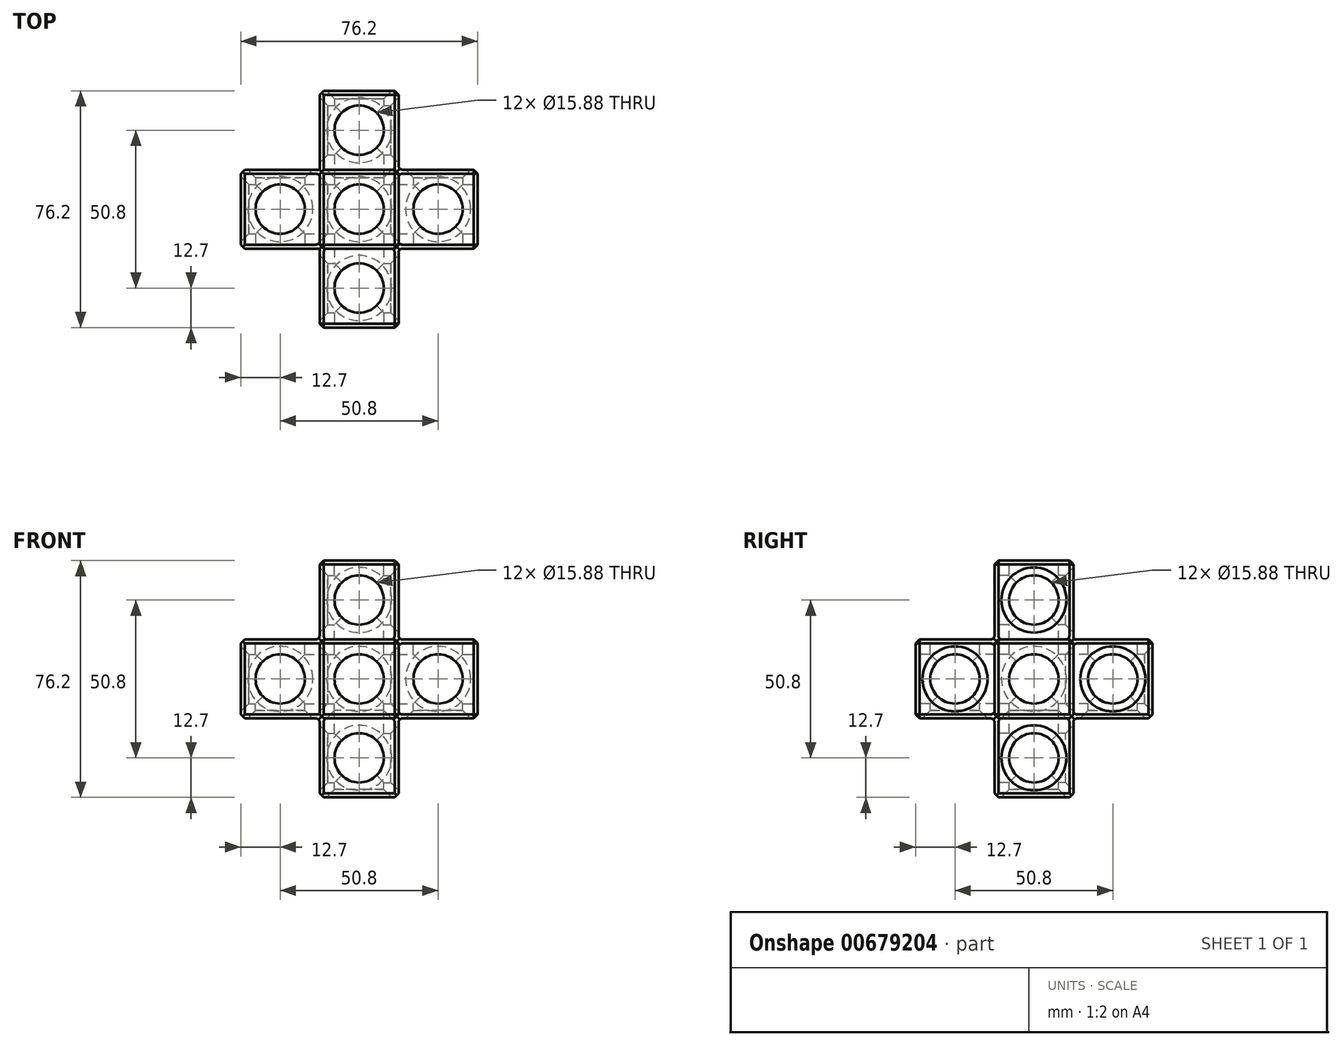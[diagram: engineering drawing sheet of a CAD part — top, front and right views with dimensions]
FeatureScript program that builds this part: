
annotation { "Feature Type Name" : "Feature", "Feature Type Description" : "" }
export const myFeature = defineFeature(function(context is Context, id is Id, definition is map)
    precondition{}
    {
        {
            var Q0;
            Q0=qCreatedBy(makeId("Front.planeOp"),FACE);
            var sketch = newSketch(context, id + "F0", { "sketchPlane" : qUnion([Q0])});
            skLineSegment(sketch, "E0", {"start": v(0, 0) * mm, "end": v(25.4, 0) * mm});
            skLineSegment(sketch, "E1", {"start": v(25.4, 0) * mm, "end": v(25.4, 25.4) * mm});
            skLineSegment(sketch, "E2", {"start": v(25.4, 25.4) * mm, "end": v(50.8, 25.4) * mm});
            skLineSegment(sketch, "E3", {"start": v(50.8, 25.4) * mm, "end": v(50.8, 0) * mm});
            skLineSegment(sketch, "E4", {"start": v(50.8, 0) * mm, "end": v(76.2, 0) * mm});
            skLineSegment(sketch, "E5", {"start": v(76.2, 0) * mm, "end": v(76.2, -25.4) * mm});
            skLineSegment(sketch, "E6", {"start": v(76.2, -25.4) * mm, "end": v(50.8, -25.4) * mm});
            skLineSegment(sketch, "E7", {"start": v(50.8, -25.4) * mm, "end": v(50.8, -50.8) * mm});
            skLineSegment(sketch, "E8", {"start": v(50.8, -50.8) * mm, "end": v(25.4, -50.8) * mm});
            skLineSegment(sketch, "E9", {"start": v(25.4, -50.8) * mm, "end": v(25.4, -25.4) * mm});
            skLineSegment(sketch, "E10", {"start": v(25.4, -25.4) * mm, "end": v(0, -25.4) * mm});
            skLineSegment(sketch, "E11", {"start": v(0, -25.4) * mm, "end": v(0, 0) * mm});
            skSolve(sketch);
        }
        {
            var Q0;
            Q0 = qSketchRegion(id + "F0", true);
            extrude(context, id + "F1", {"entities" : qUnion([Q0]), "depth" : 25.4 * mm, "offsetDistance" : 25.4 * mm});
        }
        {
            var Q0;
            Q0=makeQuery(id+"F1.opExtrude","CAP_FACE",FACE,{"disambiguationData":[OSD([sQuery(id+"F0.wireOp",EDGE,"E0"),sQuery(id+"F0.wireOp",EDGE,"E1"),sQuery(id+"F0.wireOp",EDGE,"E2"),sQuery(id+"F0.wireOp",EDGE,"E3"),sQuery(id+"F0.wireOp",EDGE,"E4"),sQuery(id+"F0.wireOp",EDGE,"E5"),sQuery(id+"F0.wireOp",EDGE,"E6"),sQuery(id+"F0.wireOp",EDGE,"E7"),sQuery(id+"F0.wireOp",EDGE,"E8"),sQuery(id+"F0.wireOp",EDGE,"E9"),sQuery(id+"F0.wireOp",EDGE,"E10"),sQuery(id+"F0.wireOp",EDGE,"E11")])],"isStart":false});
            var sketch = newSketch(context, id + "F2", { "sketchPlane" : qUnion([Q0])});
            skLineSegment(sketch, "E12.bottom", {"start": v(25.4, 0) * mm, "end": v(50.8, 0) * mm});
            skLineSegment(sketch, "E12.top", {"start": v(25.4, -25.4) * mm, "end": v(50.8, -25.4) * mm});
            skLineSegment(sketch, "E12.left", {"start": v(25.4, 0) * mm, "end": v(25.4, -25.4) * mm});
            skLineSegment(sketch, "E12.right", {"start": v(50.8, 0) * mm, "end": v(50.8, -25.4) * mm});
            skSolve(sketch);
        }
        {
            var Q0;
            Q0 = qSketchRegion(id + "F2", true);
            extrude(context, id + "F3", {"entities" : qUnion([Q0]), "operationType" : NewBodyOperationType.ADD, "depth" : 25.4 * mm, "offsetDistance" : 25.4 * mm});
        }
        {
            var Q0;
            Q0=makeQuery(id+"F1.opExtrude","CAP_FACE",FACE,{"disambiguationData":[OSD([sQuery(id+"F0.wireOp",EDGE,"E0"),sQuery(id+"F0.wireOp",EDGE,"E1"),sQuery(id+"F0.wireOp",EDGE,"E2"),sQuery(id+"F0.wireOp",EDGE,"E3"),sQuery(id+"F0.wireOp",EDGE,"E4"),sQuery(id+"F0.wireOp",EDGE,"E5"),sQuery(id+"F0.wireOp",EDGE,"E6"),sQuery(id+"F0.wireOp",EDGE,"E7"),sQuery(id+"F0.wireOp",EDGE,"E8"),sQuery(id+"F0.wireOp",EDGE,"E9"),sQuery(id+"F0.wireOp",EDGE,"E10"),sQuery(id+"F0.wireOp",EDGE,"E11")])],"isStart":true});
            var sketch = newSketch(context, id + "F4", { "sketchPlane" : qUnion([Q0])});
            skLineSegment(sketch, "E13.bottom", {"start": v(-50.8, 0) * mm, "end": v(-25.4, 0) * mm});
            skLineSegment(sketch, "E13.top", {"start": v(-50.8, -25.4) * mm, "end": v(-25.4, -25.4) * mm});
            skLineSegment(sketch, "E13.left", {"start": v(-50.8, 0) * mm, "end": v(-50.8, -25.4) * mm});
            skLineSegment(sketch, "E13.right", {"start": v(-25.4, 0) * mm, "end": v(-25.4, -25.4) * mm});
            skSolve(sketch);
        }
        {
            var Q0;
            Q0 = qSketchRegion(id + "F4", true);
            extrude(context, id + "F5", {"entities" : qUnion([Q0]), "operationType" : NewBodyOperationType.ADD, "depth" : 25.4 * mm, "offsetDistance" : 25.4 * mm});
        }
        {
            var Q0;
            Q0=makeQuery(id+"F3.opExtrude","CAP_FACE",FACE,{"disambiguationData":[OSD([sQuery(id+"F2.wireOp",EDGE,"E12.bottom"),sQuery(id+"F2.wireOp",EDGE,"E12.top"),sQuery(id+"F2.wireOp",EDGE,"E12.left"),sQuery(id+"F2.wireOp",EDGE,"E12.right")])],"isStart":false});
            var sketch = newSketch(context, id + "F6", { "sketchPlane" : qUnion([Q0])});
            skCircle(sketch, "E14", {"center": v(38.1, -12.7) * mm, "radius": 7.94 * mm});
            skSolve(sketch);
        }
        {
            var Q0;
            Q0 = qSketchRegion(id + "F6", true);
            extrude(context, id + "F7", {"entities" : qUnion([Q0]), "operationType" : NewBodyOperationType.REMOVE, "endBound" : BoundingType.THROUGH_ALL, "oppositeDirection" : true, "depth" : 25.4 * mm, "offsetDistance" : 25.4 * mm});
        }
        {
            var Q0;
            Q0=makeQuery(id+"F1.opExtrude","SWEPT_FACE",FACE,{"disambiguationData":[OSD([sQuery(id+"F0.wireOp",EDGE,"E2")])]});
            var sketch = newSketch(context, id + "F8", { "sketchPlane" : qUnion([Q0])});
            skCircle(sketch, "E15", {"center": v(38.1, -12.7) * mm, "radius": 7.94 * mm});
            skSolve(sketch);
        }
        {
            var Q0;
            Q0 = qSketchRegion(id + "F8", true);
            extrude(context, id + "F9", {"entities" : qUnion([Q0]), "operationType" : NewBodyOperationType.REMOVE, "endBound" : BoundingType.THROUGH_ALL, "oppositeDirection" : true, "depth" : 25.4 * mm, "offsetDistance" : 25.4 * mm});
        }
        {
            var Q0;
            {var subQ0=sQuery(id+"F0.wireOp",EDGE,"E2");var subQ1=sQuery(id+"F0.wireOp",EDGE,"E1");var subQ2=sQuery(id+"F0.wireOp",EDGE,"E4");var subQ3=sQuery(id+"F0.wireOp",EDGE,"E3");var subQ4=sQuery(id+"F0.wireOp",EDGE,"E0");var subQ5=makeQuery(id+"F1.opExtrude","CAP_FACE",FACE,{"disambiguationData":[OSD([subQ4,subQ1,subQ0,subQ3,subQ2,sQuery(id+"F0.wireOp",EDGE,"E5"),sQuery(id+"F0.wireOp",EDGE,"E6"),sQuery(id+"F0.wireOp",EDGE,"E7"),sQuery(id+"F0.wireOp",EDGE,"E8"),sQuery(id+"F0.wireOp",EDGE,"E9"),sQuery(id+"F0.wireOp",EDGE,"E10"),sQuery(id+"F0.wireOp",EDGE,"E11")])],"isStart":false});Q0=makeQuery(id+"F3.boolean.opBoolean","SPLIT",FACE,{"disambiguationData":[TD([makeQuery(id+"F1.opExtrude","SWEPT_FACE",FACE,{"disambiguationData":[OSD([subQ0])]})])],"derivedFrom":subQ5});}
            var sketch = newSketch(context, id + "F10", { "sketchPlane" : qUnion([Q0])});
            skCircle(sketch, "E16", {"center": v(38.1, 12.7) * mm, "radius": 7.94 * mm});
            skCircle(sketch, "E17", {"center": v(63.5, -12.7) * mm, "radius": 7.94 * mm});
            skCircle(sketch, "E18", {"center": v(38.1, -38.1) * mm, "radius": 7.94 * mm});
            skCircle(sketch, "E19", {"center": v(12.7, -12.7) * mm, "radius": 7.94 * mm});
            skSolve(sketch);
        }
        {
            var Q0;
            Q0 = qSketchRegion(id + "F10", true);
            extrude(context, id + "F11", {"entities" : qUnion([Q0]), "operationType" : NewBodyOperationType.REMOVE, "endBound" : BoundingType.THROUGH_ALL, "oppositeDirection" : true, "depth" : 25.4 * mm, "offsetDistance" : 25.4 * mm});
        }
        {
            var Q0;
            Q0=makeQuery(id+"F1.opExtrude","SWEPT_FACE",FACE,{"disambiguationData":[OSD([sQuery(id+"F0.wireOp",EDGE,"E0")])]});
            var sketch = newSketch(context, id + "F12", { "sketchPlane" : qUnion([Q0])});
            skCircle(sketch, "E20", {"center": v(12.7, -12.7) * mm, "radius": 7.94 * mm});
            skPoint(sketch, "E20.centerSnap0", {"position": v(0, -12.7) * mm});
            skCircle(sketch, "E21", {"center": v(63.5, -12.7) * mm, "radius": 7.94 * mm});
            skCircle(sketch, "E22", {"center": v(38.1, -38.1) * mm, "radius": 7.94 * mm});
            skCircle(sketch, "E23", {"center": v(38.1, 12.7) * mm, "radius": 7.94 * mm});
            skSolve(sketch);
        }
        {
            var Q0;
            Q0 = qSketchRegion(id + "F12", true);
            extrude(context, id + "F13", {"entities" : qUnion([Q0]), "operationType" : NewBodyOperationType.REMOVE, "endBound" : BoundingType.THROUGH_ALL, "oppositeDirection" : true, "depth" : 25.4 * mm, "offsetDistance" : 25.4 * mm});
        }
        {
            var Q0;
            Q0=makeQuery(id+"F1.opExtrude","SWEPT_FACE",FACE,{"disambiguationData":[OSD([sQuery(id+"F0.wireOp",EDGE,"E5")])]});
            var sketch = newSketch(context, id + "F14", { "sketchPlane" : qUnion([Q0])});
            skCircle(sketch, "E24", {"center": v(-12.7, -12.7) * mm, "radius": 7.94 * mm});
            skPoint(sketch, "E24.centerSnap0", {"position": v(-12.7, 0) * mm});
            skPoint(sketch, "E24.centerSnap1", {"position": v(-25.4, -12.7) * mm});
            skCircle(sketch, "E25", {"center": v(-12.7, 12.7) * mm, "radius": 7.94 * mm});
            skCircle(sketch, "E26", {"center": v(-38.1, -12.7) * mm, "radius": 7.94 * mm});
            skCircle(sketch, "E27", {"center": v(12.7, -12.7) * mm, "radius": 7.94 * mm});
            skCircle(sketch, "E28", {"center": v(-12.7, -38.1) * mm, "radius": 7.94 * mm});
            skSolve(sketch);
        }
        {
            var Q0;
            Q0 = qSketchRegion(id + "F14", true);
            extrude(context, id + "F15", {"entities" : qUnion([Q0]), "operationType" : NewBodyOperationType.REMOVE, "endBound" : BoundingType.THROUGH_ALL, "oppositeDirection" : true, "depth" : 25.4 * mm, "offsetDistance" : 25.4 * mm});
        }
        {
            var Q0;
            Q0=makeQuery(id+"F9.boolean.opBoolean","COPY",EDGE,{"derivedFrom":makeQuery(id+"F9.opExtrude","CAP_EDGE",EDGE,{"disambiguationData":[OSD([sQuery(id+"F8.wireOp",EDGE,"E15")])],"isStart":true})});
            var Q1;
            Q1=makeQuery(id+"F11.boolean.opBoolean","COPY",EDGE,{"derivedFrom":makeQuery(id+"F11.opExtrude","CAP_EDGE",EDGE,{"disambiguationData":[OSD([sQuery(id+"F10.wireOp",EDGE,"E16")])],"isStart":true})});
            var Q2;
            Q2=makeQuery(id+"F15.boolean.opBoolean","INTERSECT",EDGE,{"derivedFrom":[makeQuery(id+"F1.opExtrude","SWEPT_FACE",FACE,{"disambiguationData":[OSD([sQuery(id+"F0.wireOp",EDGE,"E3")])]}),makeQuery(id+"F15.opExtrude","SWEPT_FACE",FACE,{"disambiguationData":[OSD([sQuery(id+"F14.wireOp",EDGE,"E25")])]})]});
            var Q3;
            Q3=makeQuery(id+"F13.boolean.opBoolean","COPY",EDGE,{"derivedFrom":makeQuery(id+"F13.opExtrude","CAP_EDGE",EDGE,{"disambiguationData":[OSD([sQuery(id+"F12.wireOp",EDGE,"E22")])],"isStart":true})});
            var Q4;
            Q4=makeQuery(id+"F7.boolean.opBoolean","COPY",EDGE,{"derivedFrom":makeQuery(id+"F7.opExtrude","CAP_EDGE",EDGE,{"disambiguationData":[OSD([sQuery(id+"F6.wireOp",EDGE,"E14")])],"isStart":true})});
            var Q5;
            Q5=makeQuery(id+"F15.boolean.opBoolean","INTERSECT",EDGE,{"derivedFrom":[makeQuery(id+"F3.opExtrude","SWEPT_FACE",FACE,{"disambiguationData":[OSD([sQuery(id+"F2.wireOp",EDGE,"E12.right")])]}),makeQuery(id+"F15.opExtrude","SWEPT_FACE",FACE,{"disambiguationData":[OSD([sQuery(id+"F14.wireOp",EDGE,"E26")])]})]});
            var Q6;
            Q6=makeQuery(id+"F11.boolean.opBoolean","COPY",EDGE,{"derivedFrom":makeQuery(id+"F11.opExtrude","CAP_EDGE",EDGE,{"disambiguationData":[OSD([sQuery(id+"F10.wireOp",EDGE,"E18")])],"isStart":true})});
            var Q7;
            Q7=makeQuery(id+"F15.boolean.opBoolean","INTERSECT",EDGE,{"derivedFrom":[makeQuery(id+"F1.opExtrude","SWEPT_FACE",FACE,{"disambiguationData":[OSD([sQuery(id+"F0.wireOp",EDGE,"E7")])]}),makeQuery(id+"F15.opExtrude","SWEPT_FACE",FACE,{"disambiguationData":[OSD([sQuery(id+"F14.wireOp",EDGE,"E28")])]})]});
            var Q8;
            Q8=makeQuery(id+"F15.boolean.opBoolean","COPY",EDGE,{"derivedFrom":makeQuery(id+"F15.opExtrude","CAP_EDGE",EDGE,{"disambiguationData":[OSD([sQuery(id+"F14.wireOp",EDGE,"E24")])],"isStart":true})});
            var Q9;
            Q9=makeQuery(id+"F11.boolean.opBoolean","COPY",EDGE,{"derivedFrom":makeQuery(id+"F11.opExtrude","CAP_EDGE",EDGE,{"disambiguationData":[OSD([sQuery(id+"F10.wireOp",EDGE,"E17")])],"isStart":true})});
            var Q10;
            Q10=makeQuery(id+"F15.boolean.opBoolean","INTERSECT",EDGE,{"derivedFrom":[makeQuery(id+"F5.opExtrude","SWEPT_FACE",FACE,{"disambiguationData":[OSD([sQuery(id+"F4.wireOp",EDGE,"E13.left")])]}),makeQuery(id+"F15.opExtrude","SWEPT_FACE",FACE,{"disambiguationData":[OSD([sQuery(id+"F14.wireOp",EDGE,"E27")])]})]});
            var Q11;
            Q11=makeQuery(id+"F13.boolean.opBoolean","COPY",EDGE,{"derivedFrom":makeQuery(id+"F13.opExtrude","CAP_EDGE",EDGE,{"disambiguationData":[OSD([sQuery(id+"F12.wireOp",EDGE,"E23")])],"isStart":true})});
            var Q12;
            Q12=makeQuery(id+"F13.boolean.opBoolean","COPY",EDGE,{"derivedFrom":makeQuery(id+"F13.opExtrude","CAP_EDGE",EDGE,{"disambiguationData":[OSD([sQuery(id+"F12.wireOp",EDGE,"E21")])],"isStart":true})});
            var Q13;
            Q13=makeQuery(id+"F13.boolean.opBoolean","COPY",EDGE,{"derivedFrom":makeQuery(id+"F13.opExtrude","CAP_EDGE",EDGE,{"disambiguationData":[OSD([sQuery(id+"F12.wireOp",EDGE,"E20")])],"isStart":true})});
            var Q14;
            Q14=makeQuery(id+"F11.boolean.opBoolean","COPY",EDGE,{"derivedFrom":makeQuery(id+"F11.opExtrude","CAP_EDGE",EDGE,{"disambiguationData":[OSD([sQuery(id+"F10.wireOp",EDGE,"E19")])],"isStart":true})});
            chamfer(context, id + "F16", {"entities" : qUnion([Q0, Q1, Q2, Q3, Q4, Q5, Q6, Q7, Q8, Q9, Q10, Q11, Q12, Q13, Q14]), "width" : 2.54 * mm, "tangentPropagation" : true});
        }
        {
            var Q0;
            Q0=makeQuery(id+"F15.boolean.opBoolean","INTERSECT",EDGE,{"derivedFrom":[makeQuery(id+"F1.opExtrude","SWEPT_FACE",FACE,{"disambiguationData":[OSD([sQuery(id+"F0.wireOp",EDGE,"E1")])]}),makeQuery(id+"F15.opExtrude","SWEPT_FACE",FACE,{"disambiguationData":[OSD([sQuery(id+"F14.wireOp",EDGE,"E25")])]})]});
            var Q1;
            Q1=makeQuery(id+"F15.boolean.opBoolean","INTERSECT",EDGE,{"derivedFrom":[makeQuery(id+"F1.opExtrude","SWEPT_FACE",FACE,{"disambiguationData":[OSD([sQuery(id+"F0.wireOp",EDGE,"E11")])]}),makeQuery(id+"F15.opExtrude","SWEPT_FACE",FACE,{"disambiguationData":[OSD([sQuery(id+"F14.wireOp",EDGE,"E24")])]})]});
            var Q2;
            Q2=makeQuery(id+"F15.boolean.opBoolean","INTERSECT",EDGE,{"derivedFrom":[makeQuery(id+"F1.opExtrude","SWEPT_FACE",FACE,{"disambiguationData":[OSD([sQuery(id+"F0.wireOp",EDGE,"E9")])]}),makeQuery(id+"F15.opExtrude","SWEPT_FACE",FACE,{"disambiguationData":[OSD([sQuery(id+"F14.wireOp",EDGE,"E28")])]})]});
            var Q3;
            Q3=makeQuery(id+"F15.boolean.opBoolean","INTERSECT",EDGE,{"derivedFrom":[makeQuery(id+"F3.opExtrude","SWEPT_FACE",FACE,{"disambiguationData":[OSD([sQuery(id+"F2.wireOp",EDGE,"E12.left")])]}),makeQuery(id+"F15.opExtrude","SWEPT_FACE",FACE,{"disambiguationData":[OSD([sQuery(id+"F14.wireOp",EDGE,"E26")])]})]});
            chamfer(context, id + "F17", {"entities" : qUnion([Q0, Q1, Q2, Q3]), "width" : 2.54 * mm, "tangentPropagation" : true});
        }
        {
            var Q0;
            {var subQ0=sQuery(id+"F0.wireOp",EDGE,"E5");var subQ1=sQuery(id+"F0.wireOp",EDGE,"E3");var subQ2=sQuery(id+"F0.wireOp",EDGE,"E4");var subQ3=sQuery(id+"F0.wireOp",EDGE,"E7");var subQ4=sQuery(id+"F0.wireOp",EDGE,"E6");var subQ5=makeQuery(id+"F1.opExtrude","CAP_FACE",FACE,{"disambiguationData":[OSD([sQuery(id+"F0.wireOp",EDGE,"E0"),sQuery(id+"F0.wireOp",EDGE,"E1"),sQuery(id+"F0.wireOp",EDGE,"E2"),subQ1,subQ2,subQ0,subQ4,subQ3,sQuery(id+"F0.wireOp",EDGE,"E8"),sQuery(id+"F0.wireOp",EDGE,"E9"),sQuery(id+"F0.wireOp",EDGE,"E10"),sQuery(id+"F0.wireOp",EDGE,"E11")])],"isStart":true});Q0=makeQuery(id+"F11.boolean.opBoolean","INTERSECT",EDGE,{"derivedFrom":[makeQuery(id+"F5.boolean.opBoolean","SPLIT",FACE,{"disambiguationData":[TD([makeQuery(id+"F1.opExtrude","SWEPT_FACE",FACE,{"disambiguationData":[OSD([subQ0])]})])],"derivedFrom":subQ5}),makeQuery(id+"F11.opExtrude","SWEPT_FACE",FACE,{"disambiguationData":[OSD([sQuery(id+"F10.wireOp",EDGE,"E17")])]})]});}
            var Q1;
            Q1=makeQuery(id+"F13.boolean.opBoolean","INTERSECT",EDGE,{"derivedFrom":[makeQuery(id+"F1.opExtrude","SWEPT_FACE",FACE,{"disambiguationData":[OSD([sQuery(id+"F0.wireOp",EDGE,"E6")])]}),makeQuery(id+"F13.opExtrude","SWEPT_FACE",FACE,{"disambiguationData":[OSD([sQuery(id+"F12.wireOp",EDGE,"E21")])]})]});
            var Q2;
            Q2=makeQuery(id+"F9.boolean.opBoolean","INTERSECT",EDGE,{"derivedFrom":[makeQuery(id+"F1.opExtrude","SWEPT_FACE",FACE,{"disambiguationData":[OSD([sQuery(id+"F0.wireOp",EDGE,"E8")])]}),makeQuery(id+"F9.opExtrude","SWEPT_FACE",FACE,{"disambiguationData":[OSD([sQuery(id+"F8.wireOp",EDGE,"E15")])]})]});
            var Q3;
            {var subQ0=sQuery(id+"F0.wireOp",EDGE,"E8");var subQ1=sQuery(id+"F0.wireOp",EDGE,"E7");var subQ2=sQuery(id+"F0.wireOp",EDGE,"E6");var subQ3=sQuery(id+"F0.wireOp",EDGE,"E10");var subQ4=sQuery(id+"F0.wireOp",EDGE,"E9");var subQ5=makeQuery(id+"F1.opExtrude","CAP_FACE",FACE,{"disambiguationData":[OSD([sQuery(id+"F0.wireOp",EDGE,"E0"),sQuery(id+"F0.wireOp",EDGE,"E1"),sQuery(id+"F0.wireOp",EDGE,"E2"),sQuery(id+"F0.wireOp",EDGE,"E3"),sQuery(id+"F0.wireOp",EDGE,"E4"),sQuery(id+"F0.wireOp",EDGE,"E5"),subQ2,subQ1,subQ0,subQ4,subQ3,sQuery(id+"F0.wireOp",EDGE,"E11")])],"isStart":true});Q3=makeQuery(id+"F11.boolean.opBoolean","INTERSECT",EDGE,{"derivedFrom":[makeQuery(id+"F5.boolean.opBoolean","SPLIT",FACE,{"disambiguationData":[TD([makeQuery(id+"F1.opExtrude","SWEPT_FACE",FACE,{"disambiguationData":[OSD([subQ0])]})])],"derivedFrom":subQ5}),makeQuery(id+"F11.opExtrude","SWEPT_FACE",FACE,{"disambiguationData":[OSD([sQuery(id+"F10.wireOp",EDGE,"E18")])]})]});}
            var Q4;
            Q4=makeQuery(id+"F13.boolean.opBoolean","INTERSECT",EDGE,{"derivedFrom":[makeQuery(id+"F5.opExtrude","SWEPT_FACE",FACE,{"disambiguationData":[OSD([sQuery(id+"F4.wireOp",EDGE,"E13.top")])]}),makeQuery(id+"F13.opExtrude","SWEPT_FACE",FACE,{"disambiguationData":[OSD([sQuery(id+"F12.wireOp",EDGE,"E23")])]})]});
            var Q5;
            Q5=makeQuery(id+"F15.boolean.opBoolean","INTERSECT",EDGE,{"derivedFrom":[makeQuery(id+"F5.opExtrude","SWEPT_FACE",FACE,{"disambiguationData":[OSD([sQuery(id+"F4.wireOp",EDGE,"E13.right")])]}),makeQuery(id+"F15.opExtrude","SWEPT_FACE",FACE,{"disambiguationData":[OSD([sQuery(id+"F14.wireOp",EDGE,"E27")])]})]});
            var Q6;
            {var subQ0=sQuery(id+"F0.wireOp",EDGE,"E2");var subQ1=sQuery(id+"F0.wireOp",EDGE,"E1");var subQ2=sQuery(id+"F0.wireOp",EDGE,"E4");var subQ3=sQuery(id+"F0.wireOp",EDGE,"E3");var subQ4=sQuery(id+"F0.wireOp",EDGE,"E0");var subQ5=makeQuery(id+"F1.opExtrude","CAP_FACE",FACE,{"disambiguationData":[OSD([subQ4,subQ1,subQ0,subQ3,subQ2,sQuery(id+"F0.wireOp",EDGE,"E5"),sQuery(id+"F0.wireOp",EDGE,"E6"),sQuery(id+"F0.wireOp",EDGE,"E7"),sQuery(id+"F0.wireOp",EDGE,"E8"),sQuery(id+"F0.wireOp",EDGE,"E9"),sQuery(id+"F0.wireOp",EDGE,"E10"),sQuery(id+"F0.wireOp",EDGE,"E11")])],"isStart":true});Q6=makeQuery(id+"F11.boolean.opBoolean","INTERSECT",EDGE,{"derivedFrom":[makeQuery(id+"F5.boolean.opBoolean","SPLIT",FACE,{"disambiguationData":[TD([makeQuery(id+"F1.opExtrude","SWEPT_FACE",FACE,{"disambiguationData":[OSD([subQ0])]})])],"derivedFrom":subQ5}),makeQuery(id+"F11.opExtrude","SWEPT_FACE",FACE,{"disambiguationData":[OSD([sQuery(id+"F10.wireOp",EDGE,"E16")])]})]});}
            var Q7;
            {var subQ0=sQuery(id+"F0.wireOp",EDGE,"E1");var subQ1=sQuery(id+"F0.wireOp",EDGE,"E9");var subQ2=sQuery(id+"F0.wireOp",EDGE,"E0");var subQ3=sQuery(id+"F0.wireOp",EDGE,"E11");var subQ4=sQuery(id+"F0.wireOp",EDGE,"E10");var subQ5=makeQuery(id+"F1.opExtrude","CAP_FACE",FACE,{"disambiguationData":[OSD([subQ2,subQ0,sQuery(id+"F0.wireOp",EDGE,"E2"),sQuery(id+"F0.wireOp",EDGE,"E3"),sQuery(id+"F0.wireOp",EDGE,"E4"),sQuery(id+"F0.wireOp",EDGE,"E5"),sQuery(id+"F0.wireOp",EDGE,"E6"),sQuery(id+"F0.wireOp",EDGE,"E7"),sQuery(id+"F0.wireOp",EDGE,"E8"),subQ1,subQ4,subQ3])],"isStart":true});Q7=makeQuery(id+"F11.boolean.opBoolean","INTERSECT",EDGE,{"derivedFrom":[makeQuery(id+"F5.boolean.opBoolean","SPLIT",FACE,{"disambiguationData":[TD([makeQuery(id+"F1.opExtrude","SWEPT_FACE",FACE,{"disambiguationData":[OSD([subQ3])]})])],"derivedFrom":subQ5}),makeQuery(id+"F11.opExtrude","SWEPT_FACE",FACE,{"disambiguationData":[OSD([sQuery(id+"F10.wireOp",EDGE,"E19")])]})]});}
            var Q8;
            Q8=makeQuery(id+"F13.boolean.opBoolean","INTERSECT",EDGE,{"derivedFrom":[makeQuery(id+"F1.opExtrude","SWEPT_FACE",FACE,{"disambiguationData":[OSD([sQuery(id+"F0.wireOp",EDGE,"E10")])]}),makeQuery(id+"F13.opExtrude","SWEPT_FACE",FACE,{"disambiguationData":[OSD([sQuery(id+"F12.wireOp",EDGE,"E20")])]})]});
            var Q9;
            Q9=makeQuery(id+"F7.boolean.opBoolean","INTERSECT",EDGE,{"derivedFrom":[makeQuery(id+"F5.opExtrude","CAP_FACE",FACE,{"disambiguationData":[OSD([sQuery(id+"F4.wireOp",EDGE,"E13.bottom"),sQuery(id+"F4.wireOp",EDGE,"E13.top"),sQuery(id+"F4.wireOp",EDGE,"E13.left"),sQuery(id+"F4.wireOp",EDGE,"E13.right")])],"isStart":false}),makeQuery(id+"F7.opExtrude","SWEPT_FACE",FACE,{"disambiguationData":[OSD([sQuery(id+"F6.wireOp",EDGE,"E14")])]})]});
            chamfer(context, id + "F18", {"entities" : qUnion([Q0, Q1, Q2, Q3, Q4, Q5, Q6, Q7, Q8, Q9]), "width" : 2.54 * mm, "tangentPropagation" : true});
        }
        {
            var Q0;
            Q0=makeQuery(id+"F1.opExtrude","CAP_EDGE",EDGE,{"disambiguationData":[OSD([sQuery(id+"F0.wireOp",EDGE,"E2")])],"isStart":false});
            var Q1;
            Q1=makeQuery(id+"F1.opExtrude","SWEPT_EDGE",EDGE,{"disambiguationData":[OSD([sQuery(id+"F0.wireOp",EDGE,"E2"),sQuery(id+"F0.wireOp",EDGE,"E3")])]});
            var Q2;
            Q2=makeQuery(id+"F1.opExtrude","CAP_EDGE",EDGE,{"disambiguationData":[OSD([sQuery(id+"F0.wireOp",EDGE,"E2")])],"isStart":true});
            var Q3;
            Q3=makeQuery(id+"F1.opExtrude","SWEPT_EDGE",EDGE,{"disambiguationData":[OSD([sQuery(id+"F0.wireOp",EDGE,"E1"),sQuery(id+"F0.wireOp",EDGE,"E2")])]});
            var Q4;
            Q4=makeQuery(id+"F1.opExtrude","CAP_EDGE",EDGE,{"disambiguationData":[OSD([sQuery(id+"F0.wireOp",EDGE,"E3")])],"isStart":false});
            var Q5;
            Q5=makeQuery(id+"F1.opExtrude","CAP_EDGE",EDGE,{"disambiguationData":[OSD([sQuery(id+"F0.wireOp",EDGE,"E3")])],"isStart":true});
            var Q6;
            Q6=makeQuery(id+"F1.opExtrude","CAP_EDGE",EDGE,{"disambiguationData":[OSD([sQuery(id+"F0.wireOp",EDGE,"E1")])],"isStart":false});
            chamfer(context, id + "F19", {"entities" : qUnion([Q0, Q1, Q2, Q3, Q4, Q5, Q6]), "width" : 1.27 * mm, "tangentPropagation" : true});
        }
        {
            var Q0;
            Q0=makeQuery(id+"F3.opExtrude","SWEPT_EDGE",EDGE,{"disambiguationData":[OSD([sQuery(id+"F0.wireOp",EDGE,"E3"),sQuery(id+"F0.wireOp",EDGE,"E4"),sQuery(id+"F2.wireOp",EDGE,"E12.bottom"),sQuery(id+"F2.wireOp",EDGE,"E12.right")])]});
            var Q1;
            Q1=makeQuery(id+"F3.opExtrude","SWEPT_EDGE",EDGE,{"disambiguationData":[OSD([sQuery(id+"F0.wireOp",EDGE,"E0"),sQuery(id+"F0.wireOp",EDGE,"E1"),sQuery(id+"F2.wireOp",EDGE,"E12.bottom"),sQuery(id+"F2.wireOp",EDGE,"E12.left")])]});
            var Q2;
            Q2=makeQuery(id+"F3.opExtrude","CAP_EDGE",EDGE,{"disambiguationData":[OSD([sQuery(id+"F2.wireOp",EDGE,"E12.left")])],"isStart":false});
            var Q3;
            Q3=makeQuery(id+"F3.opExtrude","CAP_EDGE",EDGE,{"disambiguationData":[OSD([sQuery(id+"F2.wireOp",EDGE,"E12.bottom")])],"isStart":false});
            var Q4;
            Q4=makeQuery(id+"F3.opExtrude","CAP_EDGE",EDGE,{"disambiguationData":[OSD([sQuery(id+"F2.wireOp",EDGE,"E12.right")])],"isStart":false});
            var Q5;
            Q5=makeQuery(id+"F3.opExtrude","CAP_EDGE",EDGE,{"disambiguationData":[OSD([sQuery(id+"F2.wireOp",EDGE,"E12.top")])],"isStart":false});
            var Q6;
            Q6=makeQuery(id+"F3.opExtrude","SWEPT_EDGE",EDGE,{"disambiguationData":[OSD([sQuery(id+"F0.wireOp",EDGE,"E6"),sQuery(id+"F0.wireOp",EDGE,"E7"),sQuery(id+"F2.wireOp",EDGE,"E12.top"),sQuery(id+"F2.wireOp",EDGE,"E12.right")])]});
            chamfer(context, id + "F20", {"entities" : qUnion([Q0, Q1, Q2, Q3, Q4, Q5, Q6]), "width" : 1.27 * mm, "tangentPropagation" : true});
        }
        {
            var Q0;
            Q0=makeQuery(id+"F1.opExtrude","CAP_EDGE",EDGE,{"disambiguationData":[OSD([sQuery(id+"F0.wireOp",EDGE,"E4")])],"isStart":false});
            var Q1;
            Q1=makeQuery(id+"F1.opExtrude","CAP_EDGE",EDGE,{"disambiguationData":[OSD([sQuery(id+"F0.wireOp",EDGE,"E6")])],"isStart":false});
            var Q2;
            Q2=makeQuery(id+"F1.opExtrude","CAP_EDGE",EDGE,{"disambiguationData":[OSD([sQuery(id+"F0.wireOp",EDGE,"E5")])],"isStart":false});
            var Q3;
            Q3=makeQuery(id+"F1.opExtrude","SWEPT_EDGE",EDGE,{"disambiguationData":[OSD([sQuery(id+"F0.wireOp",EDGE,"E4"),sQuery(id+"F0.wireOp",EDGE,"E5")])]});
            var Q4;
            Q4=makeQuery(id+"F1.opExtrude","CAP_EDGE",EDGE,{"disambiguationData":[OSD([sQuery(id+"F0.wireOp",EDGE,"E5")])],"isStart":true});
            var Q5;
            Q5=makeQuery(id+"F1.opExtrude","SWEPT_EDGE",EDGE,{"disambiguationData":[OSD([sQuery(id+"F0.wireOp",EDGE,"E5"),sQuery(id+"F0.wireOp",EDGE,"E6")])]});
            var Q6;
            Q6=makeQuery(id+"F1.opExtrude","CAP_EDGE",EDGE,{"disambiguationData":[OSD([sQuery(id+"F0.wireOp",EDGE,"E4")])],"isStart":true});
            var Q7;
            Q7=makeQuery(id+"F1.opExtrude","CAP_EDGE",EDGE,{"disambiguationData":[OSD([sQuery(id+"F0.wireOp",EDGE,"E0")])],"isStart":false});
            var Q8;
            Q8=makeQuery(id+"F1.opExtrude","SWEPT_EDGE",EDGE,{"disambiguationData":[OSD([sQuery(id+"F0.wireOp",EDGE,"E0"),sQuery(id+"F0.wireOp",EDGE,"E11")])]});
            var Q9;
            Q9=makeQuery(id+"F1.opExtrude","CAP_EDGE",EDGE,{"disambiguationData":[OSD([sQuery(id+"F0.wireOp",EDGE,"E0")])],"isStart":true});
            var Q10;
            Q10=makeQuery(id+"F5.opExtrude","SWEPT_EDGE",EDGE,{"disambiguationData":[OSD([sQuery(id+"F0.wireOp",EDGE,"E3"),sQuery(id+"F0.wireOp",EDGE,"E4"),sQuery(id+"F4.wireOp",EDGE,"E13.bottom"),sQuery(id+"F4.wireOp",EDGE,"E13.left")])]});
            var Q11;
            Q11=makeQuery(id+"F5.opExtrude","CAP_EDGE",EDGE,{"disambiguationData":[OSD([sQuery(id+"F4.wireOp",EDGE,"E13.left")])],"isStart":false});
            var Q12;
            Q12=makeQuery(id+"F5.opExtrude","CAP_EDGE",EDGE,{"disambiguationData":[OSD([sQuery(id+"F4.wireOp",EDGE,"E13.bottom")])],"isStart":false});
            chamfer(context, id + "F21", {"entities" : qUnion([Q0, Q1, Q2, Q3, Q4, Q5, Q6, Q7, Q8, Q9, Q10, Q11, Q12]), "width" : 1.27 * mm, "tangentPropagation" : true});
        }
        {
            var Q0;
            Q0=makeQuery(id+"F1.opExtrude","CAP_EDGE",EDGE,{"disambiguationData":[OSD([sQuery(id+"F0.wireOp",EDGE,"E11")])],"isStart":true});
            var Q1;
            Q1=makeQuery(id+"F1.opExtrude","SWEPT_EDGE",EDGE,{"disambiguationData":[OSD([sQuery(id+"F0.wireOp",EDGE,"E10"),sQuery(id+"F0.wireOp",EDGE,"E11")])]});
            var Q2;
            Q2=makeQuery(id+"F1.opExtrude","CAP_EDGE",EDGE,{"disambiguationData":[OSD([sQuery(id+"F0.wireOp",EDGE,"E11")])],"isStart":false});
            var Q3;
            Q3=makeQuery(id+"F1.opExtrude","CAP_EDGE",EDGE,{"disambiguationData":[OSD([sQuery(id+"F0.wireOp",EDGE,"E1")])],"isStart":true});
            var Q4;
            Q4=makeQuery(id+"F5.opExtrude","CAP_EDGE",EDGE,{"disambiguationData":[OSD([sQuery(id+"F4.wireOp",EDGE,"E13.right")])],"isStart":false});
            var Q5;
            Q5=makeQuery(id+"F5.opExtrude","SWEPT_EDGE",EDGE,{"disambiguationData":[OSD([sQuery(id+"F0.wireOp",EDGE,"E9"),sQuery(id+"F0.wireOp",EDGE,"E10"),sQuery(id+"F4.wireOp",EDGE,"E13.top"),sQuery(id+"F4.wireOp",EDGE,"E13.right")])]});
            var Q6;
            Q6=makeQuery(id+"F3.opExtrude","SWEPT_EDGE",EDGE,{"disambiguationData":[OSD([sQuery(id+"F0.wireOp",EDGE,"E9"),sQuery(id+"F0.wireOp",EDGE,"E10"),sQuery(id+"F2.wireOp",EDGE,"E12.top"),sQuery(id+"F2.wireOp",EDGE,"E12.left")])]});
            chamfer(context, id + "F22", {"entities" : qUnion([Q0, Q1, Q2, Q3, Q4, Q5, Q6]), "width" : 1.27 * mm, "tangentPropagation" : true});
        }
        {
            var Q0;
            Q0=makeQuery(id+"F1.opExtrude","CAP_EDGE",EDGE,{"disambiguationData":[OSD([sQuery(id+"F0.wireOp",EDGE,"E9")])],"isStart":false});
            var Q1;
            Q1=makeQuery(id+"F1.opExtrude","SWEPT_EDGE",EDGE,{"disambiguationData":[OSD([sQuery(id+"F0.wireOp",EDGE,"E8"),sQuery(id+"F0.wireOp",EDGE,"E9")])]});
            var Q2;
            Q2=makeQuery(id+"F1.opExtrude","CAP_EDGE",EDGE,{"disambiguationData":[OSD([sQuery(id+"F0.wireOp",EDGE,"E9")])],"isStart":true});
            chamfer(context, id + "F23", {"entities" : qUnion([Q0, Q1, Q2]), "width" : 1.27 * mm, "tangentPropagation" : true});
        }
        {
            var Q0;
            Q0=makeQuery(id+"F1.opExtrude","CAP_EDGE",EDGE,{"disambiguationData":[OSD([sQuery(id+"F0.wireOp",EDGE,"E10")])],"isStart":true});
            var Q1;
            Q1=makeQuery(id+"F5.opExtrude","CAP_EDGE",EDGE,{"disambiguationData":[OSD([sQuery(id+"F4.wireOp",EDGE,"E13.top")])],"isStart":false});
            var Q2;
            Q2=makeQuery(id+"F5.opExtrude","SWEPT_EDGE",EDGE,{"disambiguationData":[OSD([sQuery(id+"F0.wireOp",EDGE,"E6"),sQuery(id+"F0.wireOp",EDGE,"E7"),sQuery(id+"F4.wireOp",EDGE,"E13.top"),sQuery(id+"F4.wireOp",EDGE,"E13.left")])]});
            var Q3;
            Q3=makeQuery(id+"F1.opExtrude","CAP_EDGE",EDGE,{"disambiguationData":[OSD([sQuery(id+"F0.wireOp",EDGE,"E8")])],"isStart":true});
            var Q4;
            Q4=makeQuery(id+"F1.opExtrude","SWEPT_EDGE",EDGE,{"disambiguationData":[OSD([sQuery(id+"F0.wireOp",EDGE,"E7"),sQuery(id+"F0.wireOp",EDGE,"E8")])]});
            chamfer(context, id + "F24", {"entities" : qUnion([Q0, Q1, Q2, Q3, Q4]), "width" : 1.27 * mm, "tangentPropagation" : true});
        }
        {
            var Q0;
            Q0=makeQuery(id+"F1.opExtrude","CAP_EDGE",EDGE,{"disambiguationData":[OSD([sQuery(id+"F0.wireOp",EDGE,"E6")])],"isStart":true});
            var Q1;
            Q1=makeQuery(id+"F1.opExtrude","CAP_EDGE",EDGE,{"disambiguationData":[OSD([sQuery(id+"F0.wireOp",EDGE,"E7")])],"isStart":true});
            chamfer(context, id + "F25", {"entities" : qUnion([Q0, Q1]), "width" : 1.27 * mm, "tangentPropagation" : true});
        }
        {
            var Q0;
            Q0=makeQuery(id+"F1.opExtrude","CAP_EDGE",EDGE,{"disambiguationData":[OSD([sQuery(id+"F0.wireOp",EDGE,"E7")])],"isStart":false});
            var Q1;
            Q1=makeQuery(id+"F1.opExtrude","CAP_EDGE",EDGE,{"disambiguationData":[OSD([sQuery(id+"F0.wireOp",EDGE,"E8")])],"isStart":false});
            chamfer(context, id + "F26", {"entities" : qUnion([Q0, Q1]), "width" : 1.27 * mm, "tangentPropagation" : true});
        }
        {
            var Q0;
            Q0=makeQuery(id+"F1.opExtrude","CAP_EDGE",EDGE,{"disambiguationData":[OSD([sQuery(id+"F0.wireOp",EDGE,"E10")])],"isStart":false});
            chamfer(context, id + "F27", {"entities" : qUnion([Q0]), "width" : 1.27 * mm, "tangentPropagation" : true});
        }
        {
            var Q0;
            Q0=makeQuery(id+"F5.opExtrude","SWEPT_EDGE",EDGE,{"disambiguationData":[OSD([sQuery(id+"F0.wireOp",EDGE,"E0"),sQuery(id+"F0.wireOp",EDGE,"E1"),sQuery(id+"F4.wireOp",EDGE,"E13.bottom"),sQuery(id+"F4.wireOp",EDGE,"E13.right")])]});
            chamfer(context, id + "F28", {"entities" : qUnion([Q0]), "width" : 1.27 * mm, "tangentPropagation" : true});
        }
        {
            var Q0;
            Q0=makeQuery(id+"F3.opExtrude","CAP_EDGE",EDGE,{"disambiguationData":[OSD([sQuery(id+"F2.wireOp",EDGE,"E12.bottom")])],"isStart":true});
            var Q1;
            Q1=makeQuery(id+"F1.opExtrude","SWEPT_EDGE",EDGE,{"disambiguationData":[OSD([sQuery(id+"F0.wireOp",EDGE,"E3"),sQuery(id+"F0.wireOp",EDGE,"E4")])]});
            var Q2;
            Q2=makeQuery(id+"F3.opExtrude","CAP_EDGE",EDGE,{"disambiguationData":[OSD([sQuery(id+"F2.wireOp",EDGE,"E12.right")])],"isStart":true});
            fillet(context, id + "F29", {"entities" : qUnion([Q0, Q1, Q2]), "radius" : 1.27 * mm, "tangentPropagation" : true, "allowEdgeOverflow" : false});
        }
        {
            var Q0;
            Q0=makeQuery(id+"F3.opExtrude","CAP_EDGE",EDGE,{"disambiguationData":[OSD([sQuery(id+"F2.wireOp",EDGE,"E12.left")])],"isStart":true});
            var Q1;
            Q1=makeQuery(id+"F1.opExtrude","SWEPT_EDGE",EDGE,{"disambiguationData":[OSD([sQuery(id+"F0.wireOp",EDGE,"E0"),sQuery(id+"F0.wireOp",EDGE,"E1")])]});
            fillet(context, id + "F30", {"entities" : qUnion([Q0, Q1]), "radius" : 1.27 * mm, "tangentPropagation" : true, "allowEdgeOverflow" : false});
        }
        {
            var Q0;
            Q0=makeQuery(id+"F5.opExtrude","CAP_EDGE",EDGE,{"disambiguationData":[OSD([sQuery(id+"F4.wireOp",EDGE,"E13.top")])],"isStart":true});
            var Q1;
            Q1=makeQuery(id+"F5.opExtrude","CAP_EDGE",EDGE,{"disambiguationData":[OSD([sQuery(id+"F4.wireOp",EDGE,"E13.right")])],"isStart":true});
            var Q2;
            Q2=makeQuery(id+"F1.opExtrude","SWEPT_EDGE",EDGE,{"disambiguationData":[OSD([sQuery(id+"F0.wireOp",EDGE,"E9"),sQuery(id+"F0.wireOp",EDGE,"E10")])]});
            fillet(context, id + "F31", {"entities" : qUnion([Q0, Q1, Q2]), "radius" : 1.27 * mm, "tangentPropagation" : true, "allowEdgeOverflow" : false});
        }
        {
            var Q0;
            Q0=makeQuery(id+"F5.opExtrude","CAP_EDGE",EDGE,{"disambiguationData":[OSD([sQuery(id+"F4.wireOp",EDGE,"E13.left")])],"isStart":true});
            var Q1;
            Q1=makeQuery(id+"F1.opExtrude","SWEPT_EDGE",EDGE,{"disambiguationData":[OSD([sQuery(id+"F0.wireOp",EDGE,"E6"),sQuery(id+"F0.wireOp",EDGE,"E7")])]});
            fillet(context, id + "F32", {"entities" : qUnion([Q0, Q1]), "radius" : 1.27 * mm, "tangentPropagation" : true, "allowEdgeOverflow" : false});
        }
        {
            var Q0;
            Q0=makeQuery(id+"F3.opExtrude","CAP_EDGE",EDGE,{"disambiguationData":[OSD([sQuery(id+"F2.wireOp",EDGE,"E12.top")])],"isStart":true});
            fillet(context, id + "F33", {"entities" : qUnion([Q0]), "radius" : 1.27 * mm, "tangentPropagation" : true, "allowEdgeOverflow" : false});
        }
        {
            var Q0;
            Q0=makeQuery(id+"F13.boolean.opBoolean","INTERSECT",EDGE,{"derivedFrom":[makeQuery(id+"F3.opExtrude","SWEPT_FACE",FACE,{"disambiguationData":[OSD([sQuery(id+"F2.wireOp",EDGE,"E12.top")])]}),makeQuery(id+"F13.opExtrude","SWEPT_FACE",FACE,{"disambiguationData":[OSD([sQuery(id+"F12.wireOp",EDGE,"E22")])]})]});
            chamfer(context, id + "F34", {"entities" : qUnion([Q0]), "width" : 2.54 * mm, "tangentPropagation" : true});
        }
    });
